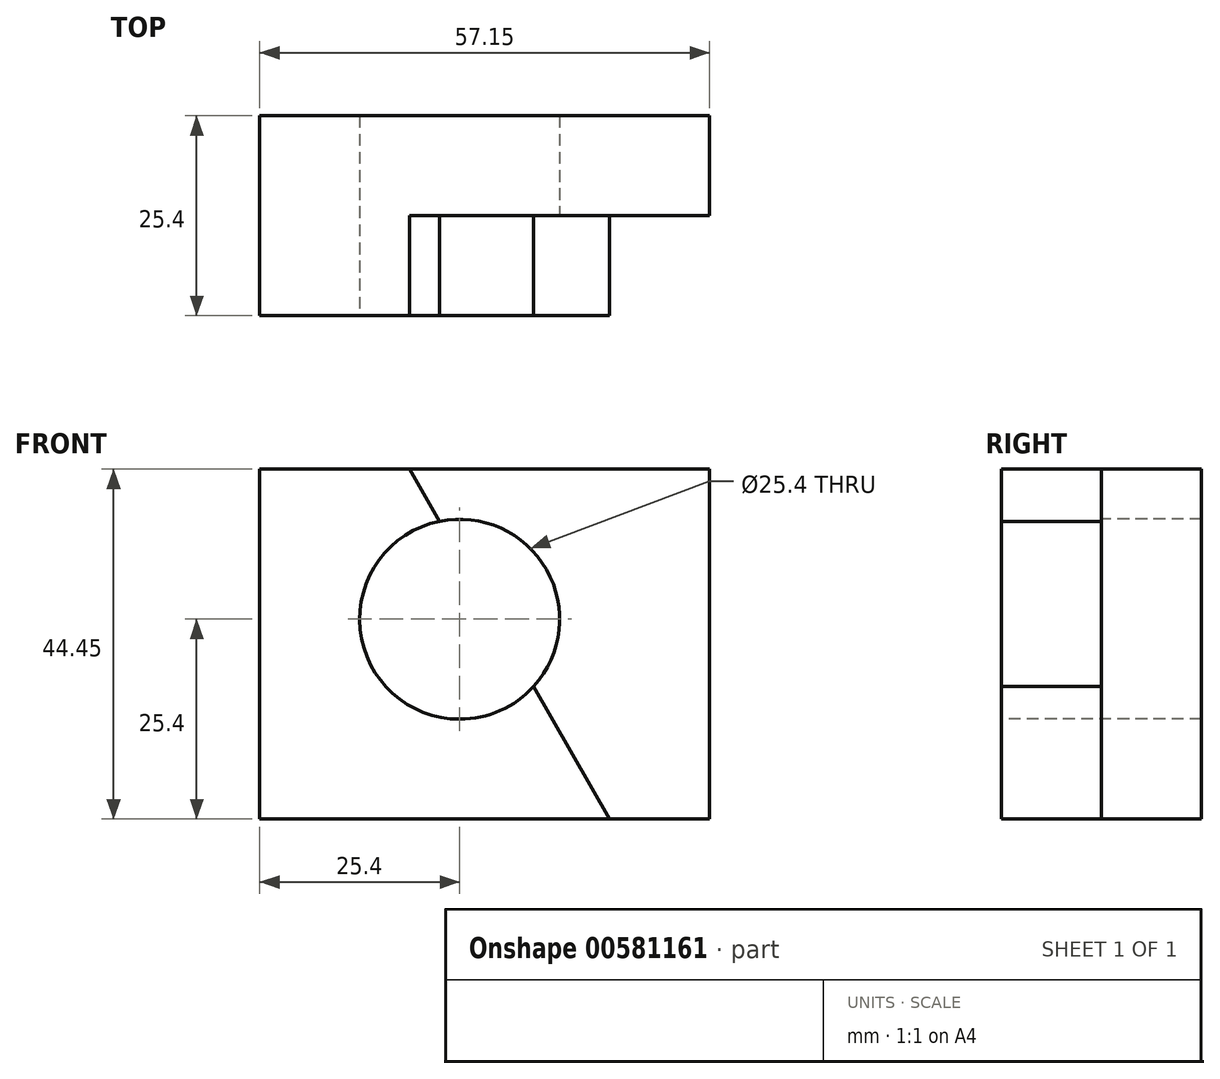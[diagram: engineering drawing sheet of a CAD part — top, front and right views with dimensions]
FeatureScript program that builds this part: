
annotation { "Feature Type Name" : "Feature", "Feature Type Description" : "" }
export const myFeature = defineFeature(function(context is Context, id is Id, definition is map)
    precondition{}
    {
        {
            var Q0;
            Q0=qCreatedBy(makeId("Front.planeOp"),FACE);
            var sketch = newSketch(context, id + "F0", { "sketchPlane" : qUnion([Q0])});
            skLineSegment(sketch, "E0", {"start": v(0, 0) * mm, "end": v(57.15, 0) * mm});
            skLineSegment(sketch, "E1", {"start": v(57.15, 0) * mm, "end": v(57.15, 44.45) * mm});
            skLineSegment(sketch, "E2", {"start": v(57.15, 44.45) * mm, "end": v(0, 44.45) * mm});
            skLineSegment(sketch, "E3", {"start": v(0, 44.45) * mm, "end": v(0, 0) * mm});
            skSolve(sketch);
        }
        {
            var Q0;
            Q0=makeQuery(id+"F0.imprint","IMPRINT",FACE,{"disambiguationData":[TD([[makeQuery(id+"F0.imprint","IMPRINT",EDGE,{"derivedFrom":sQuery(id+"F0.wireOp",EDGE,"E0")}),1.0]])]});
            extrude(context, id + "F1", {"entities" : qUnion([Q0]), "depth" : 25.4 * mm, "offsetDistance" : 25.4 * mm});
        }
        {
            var Q0;
            Q0=makeQuery(id+"F1.opExtrude","CAP_FACE",FACE,{"disambiguationData":[OSD([sQuery(id+"F0.wireOp",EDGE,"E0"),sQuery(id+"F0.wireOp",EDGE,"E1"),sQuery(id+"F0.wireOp",EDGE,"E2"),sQuery(id+"F0.wireOp",EDGE,"E3")])],"isStart":false});
            var sketch = newSketch(context, id + "F2", { "sketchPlane" : qUnion([Q0])});
            skCircle(sketch, "E4", {"center": v(25.4, 25.4) * mm, "radius": 12.7 * mm});
            skSolve(sketch);
        }
        {
            var Q0;
            Q0=makeQuery(id+"F2.imprint","IMPRINT",FACE,{"disambiguationData":[TD([[makeQuery(id+"F2.imprint","IMPRINT",EDGE,{"derivedFrom":sQuery(id+"F2.wireOp",EDGE,"E4")}),1.0]])]});
            extrude(context, id + "F3", {"entities" : qUnion([Q0]), "operationType" : NewBodyOperationType.REMOVE, "oppositeDirection" : true, "depth" : 25.4 * mm, "offsetDistance" : 25.4 * mm});
        }
        {
            var Q0;
            Q0=makeQuery(id+"F1.opExtrude","CAP_FACE",FACE,{"disambiguationData":[OSD([sQuery(id+"F0.wireOp",EDGE,"E0"),sQuery(id+"F0.wireOp",EDGE,"E1"),sQuery(id+"F0.wireOp",EDGE,"E2"),sQuery(id+"F0.wireOp",EDGE,"E3")])],"isStart":false});
            var sketch = newSketch(context, id + "F4", { "sketchPlane" : qUnion([Q0])});
            skLineSegment(sketch, "E5", {"start": v(19.05, 44.45) * mm, "end": v(44.45, 0) * mm});
            skSolve(sketch);
        }
        {
            var Q0;
            {var subQ0=makeQuery(id+"F1.opExtrude","CAP_EDGE",EDGE,{"disambiguationData":[OSD([sQuery(id+"F0.wireOp",EDGE,"E1")])],"isStart":false});Q0=makeQuery(id+"F4.imprint","IMPRINT",FACE,{"disambiguationData":[TD([[makeQuery(id+"F4.imprint","IMPRINT",EDGE,{"derivedFrom":subQ0}),1.0]])]});}
            extrude(context, id + "F5", {"entities" : qUnion([Q0]), "operationType" : NewBodyOperationType.REMOVE, "oppositeDirection" : true, "depth" : 12.7 * mm, "offsetDistance" : 25.4 * mm});
        }
    });
